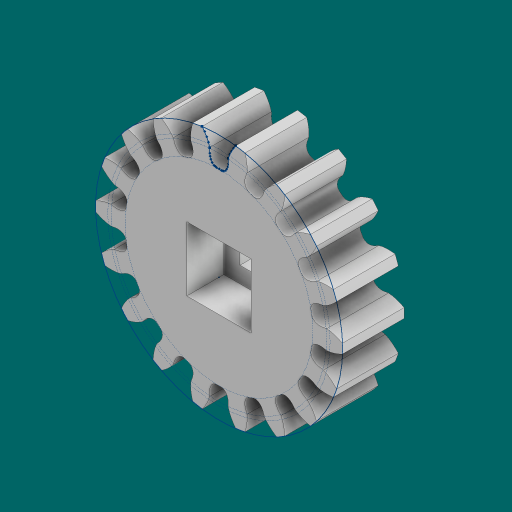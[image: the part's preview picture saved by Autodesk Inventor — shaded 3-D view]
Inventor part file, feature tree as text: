
AUTODESK INVENTOR PART (.ipt)
format: ipt  version: 2023.1 (Build 271208000, 208)  size: 325,120 bytes
history: native  units: in
note: dims shown in document units (in); Inventor stores cm internally (conversion verified against a paired STEP export)
features: extrude x5, sketch x4, pattern_circular x1, chamfer x1
ambient origin geometry x8: Origin, YZ Plane, XZ Plane, XY Plane, X Axis, Y Axis, Z Axis, Center Point
bodies: Solid1 (feature_tree)
feature tree (11):
  sketch  "Sketch1"  dims[d0=0.25in d1=0.0in]
  extrude  "Extrusion1"  TaperAngle=0.0deg  [1 undecoded]
  extrude  "Extrusion2"  Depth=7.0866in TaperAngle=360.0deg
  pattern_circular  "Circular Pattern1"  [2 undecoded]
  extrude  "Extrusion3"  Depth=0.26in
  extrude  "Extrusion4"  Depth=0.26in
  extrude  "Extrusion5"  Depth=0.05in TaperAngle=0.0deg
  chamfer  "Chamfer1"  Distance=0.33in
  sketch  "Sketch2"  dims[d2=0.0in d3=0.0in d4=7.0866in d5=360.0deg]
  sketch  "Sketch3"  dims[d7=0.13in]
  sketch  "Sketch4"  dims[d8=0.13in d9=0.0in d10=0.0in d11=0.26in d12=0.26in d13=0.15in d14=0.0in d15=0.33in d16=0.05in d17=0.0in d18=0.0118in d19=0.125in d20=45.0deg]
note: 3 required parameter values undecoded (feature->parameter linkage not recoverable at this tier; creation-order binding heuristic only, values carry confidence <= 0.55)
